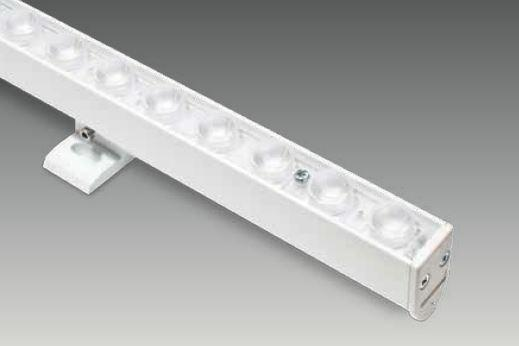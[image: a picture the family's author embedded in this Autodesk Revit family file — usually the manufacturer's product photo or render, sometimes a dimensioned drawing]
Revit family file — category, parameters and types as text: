
# Revit family: SD 1500 RUB
name_source: partatom
category: Lighting Fixtures
revit_build: Autodesk Revit 2017 (Build: 20160225_1515(x64)
units: mm (PartAtom-declared; Revit-internal decimal feet)

## family parameters
Cut with Voids When Loaded = No
Host = Face
Light Source = Yes
Part Type = Normal
Room Calculation Point = No
Round Connector Dimension = Use Diameter
Shared = No

## types (3) — shared parameters
Apparent Load = 55 VA
Color Filter = 16777215
Default Elevation = 1219 mm
Dimming Lamp Color Temperature Shift = <None>
Emit Shape Visible in Rendering = Yes
Emit from Rectangle Length = 20 mm  [stored 0.0656168 ft]
Emit from Rectangle Width = 1485 mm  [stored 4.87205 ft]
Light Source Symbol Size = 610 mm
Manufacturer = ARLIGHT
Type Image = SD 1500 RUB.JPG
Wattage Comments = 55W

## per-type parameters (varying)
| type | Beam Angle |
| SDRUB.1500.27.55.30 | 27.00° |
| SDRUB.1500.38.55.30 | 38.00° |
| SDRUB.1500.4520.55.30 | 20.00° |

note: [stored X ft] marks values corroborated as IEEE doubles in the binary element streams (Revit-internal decimal feet)

## geometry (parser evidence)
native form markers: Sweep x2
no freeform markers — native parametric forms only
